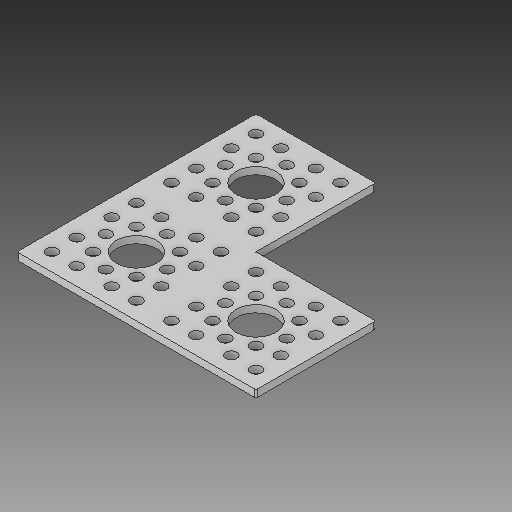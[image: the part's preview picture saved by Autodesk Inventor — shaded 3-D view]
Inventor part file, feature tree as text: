
AUTODESK INVENTOR PART (.ipt)
format: ipt  version: 2017 (Build 210142000, 142)  size: 231,936 bytes
history: native  units: in
note: dims shown in document units (in); Inventor stores cm internally (conversion verified against a paired STEP export)
features: fillet x1
ambient origin geometry x8: Origin, YZ Plane, XZ Plane, XY Plane, X Axis, Y Axis, Z Axis, Center Point
bodies: Solid1 (feature_tree)
feature tree (1):
  fillet  "Fillet1"  [1 undecoded]
note: 1 required parameter value undecoded (feature->parameter linkage not recoverable at this tier; creation-order binding heuristic only, values carry confidence <= 0.55)
